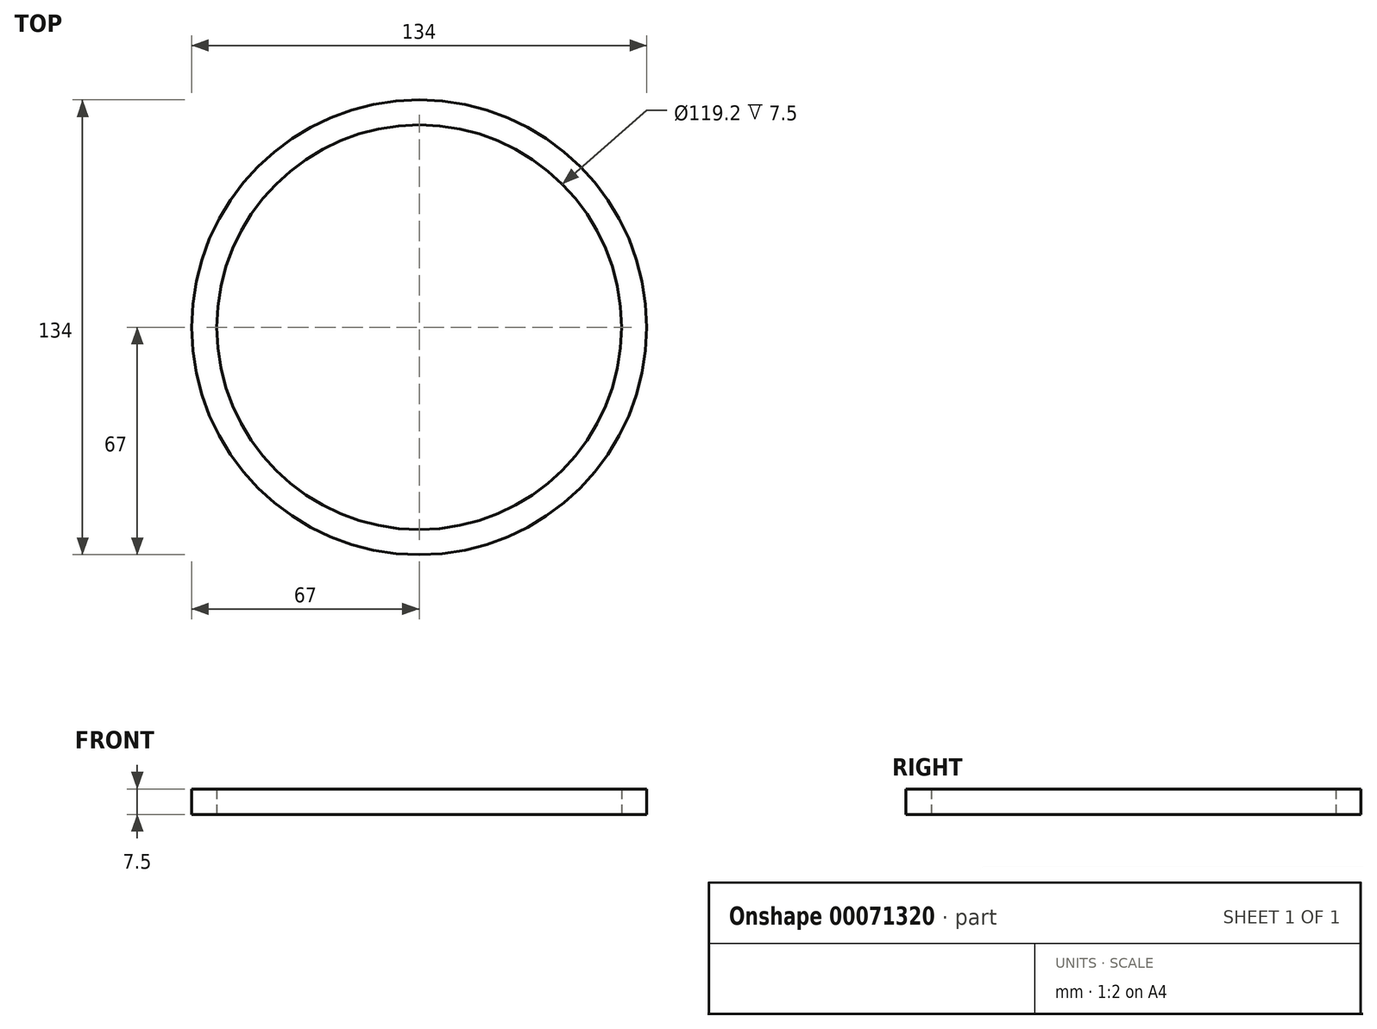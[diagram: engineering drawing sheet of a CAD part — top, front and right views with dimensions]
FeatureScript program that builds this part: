
annotation { "Feature Type Name" : "Feature", "Feature Type Description" : "" }
export const myFeature = defineFeature(function(context is Context, id is Id, definition is map)
    precondition{}
    {
        {
            var Q0;
            Q0=qCreatedBy(makeId("Top.planeOp"),FACE);
            var sketch = newSketch(context, id + "F0", { "sketchPlane" : qUnion([Q0])});
            skCircle(sketch, "E0", {"center": v(0, 0) * mm, "radius": 63.88 * mm});
            skCircle(sketch, "E1", {"center": v(0, 0) * mm, "radius": 67 * mm});
            skCircle(sketch, "E2", {"center": v(0, 0) * mm, "radius": 59.6 * mm});
            skCircle(sketch, "E3", {"center": v(0, 0) * mm, "radius": 63.12 * mm});
            skSolve(sketch);
        }
        {
            var Q0;
            Q0=makeQuery(id+"F0.imprint","IMPRINT",FACE,{"disambiguationData":[TD([[makeQuery(id+"F0.imprint","IMPRINT",EDGE,{"derivedFrom":sQuery(id+"F0.wireOp",EDGE,"E2")}),-1.0]])]});
            var Q1;
            Q1=makeQuery(id+"F0.imprint","IMPRINT",FACE,{"disambiguationData":[TD([[makeQuery(id+"F0.imprint","IMPRINT",EDGE,{"derivedFrom":sQuery(id+"F0.wireOp",EDGE,"E0")}),-1.0]])]});
            var Q2;
            Q2=makeQuery(id+"F0.imprint","IMPRINT",FACE,{"disambiguationData":[TD([[makeQuery(id+"F0.imprint","IMPRINT",EDGE,{"derivedFrom":sQuery(id+"F0.wireOp",EDGE,"E0")}),1.0]])]});
            extrude(context, id + "F1", {"entities" : qUnion([Q0, Q1, Q2]), "endBound" : BoundingType.SYMMETRIC, "depth" : 7.5 * mm});
        }
    });
